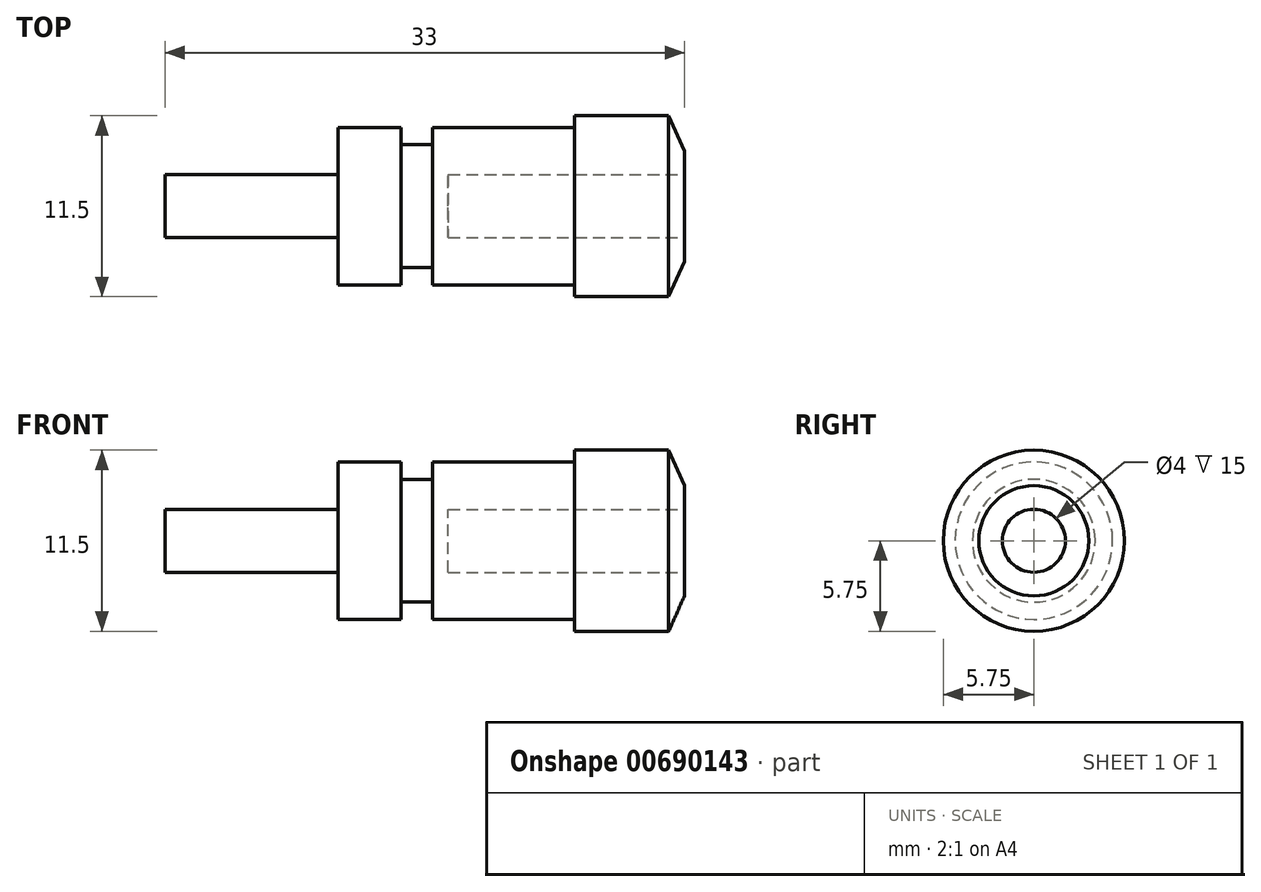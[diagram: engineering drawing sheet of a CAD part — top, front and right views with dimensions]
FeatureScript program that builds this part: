
annotation { "Feature Type Name" : "Feature", "Feature Type Description" : "" }
export const myFeature = defineFeature(function(context is Context, id is Id, definition is map)
    precondition{}
    {
        {
            var Q0;
            Q0=qCreatedBy(makeId("Front.planeOp"),FACE);
            var sketch = newSketch(context, id + "F0", { "sketchPlane" : qUnion([Q0])});
            skLineSegment(sketch, "E0", {"start": v(-17, 0) * mm, "end": v(-17, 2) * mm});
            skLineSegment(sketch, "E1", {"start": v(-17, 2) * mm, "end": v(-2, 2) * mm});
            skLineSegment(sketch, "E2", {"start": v(-2, 2) * mm, "end": v(-2, 3.9) * mm});
            skLineSegment(sketch, "E3", {"start": v(-2, 3.9) * mm, "end": v(0, 3.9) * mm});
            skLineSegment(sketch, "E4", {"start": v(0, 3.9) * mm, "end": v(0, 5) * mm});
            skLineSegment(sketch, "E5", {"start": v(0, 5) * mm, "end": v(9, 5) * mm});
            skLineSegment(sketch, "E6", {"start": v(9, 5) * mm, "end": v(9, 5.75) * mm});
            skLineSegment(sketch, "E7", {"start": v(9, 5.75) * mm, "end": v(15, 5.75) * mm});
            skLineSegment(sketch, "E8", {"start": v(15, 5.75) * mm, "end": v(16, 3.5) * mm});
            skLineSegment(sketch, "E9", {"start": v(16, 3.5) * mm, "end": v(16, 2) * mm});
            skLineSegment(sketch, "E10", {"start": v(16, 2) * mm, "end": v(1, 2) * mm});
            skLineSegment(sketch, "E11", {"start": v(1, 2) * mm, "end": v(1, 0) * mm});
            skLineSegment(sketch, "E12", {"start": v(1, 0) * mm, "end": v(-17, 0) * mm});
            skLineSegment(sketch, "E13.bottom", {"start": v(-6, 5) * mm, "end": v(-2, 5) * mm});
            skLineSegment(sketch, "E13.top", {"start": v(-6, 2) * mm, "end": v(-2, 2) * mm});
            skLineSegment(sketch, "E13.left", {"start": v(-6, 5) * mm, "end": v(-6, 2) * mm});
            skLineSegment(sketch, "E13.right", {"start": v(-2, 5) * mm, "end": v(-2, 2) * mm});
            skSolve(sketch);
        }
        {
            var Q0;
            Q0 = qSketchRegion(id + "F0", true);
            var Q1;
            Q1=sQuery(id+"F0.wireOp",EDGE,"E12");
            revolve(context, id + "F1", {"surfaceOperationType" : NewSurfaceOperationType.NEW, "entities" : qUnion([Q0]), "axis" : qUnion([Q1]), "revolveType" : RevolveType.FULL});
        }
    });
